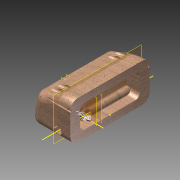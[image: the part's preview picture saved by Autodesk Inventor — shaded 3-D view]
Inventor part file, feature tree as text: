
AUTODESK INVENTOR PART (.ipt)
format: ipt  version: 2015 (Build 190159000, 159)  size: 325,120 bytes
history: native  units: in
note: dims shown in document units (in); Inventor stores cm internally (conversion verified against a paired STEP export)
features: extrude x8, sketch x6, fillet x4, plane x4, hole x2, reference x2, projected_geometry x1
ambient origin geometry x8: Origin, YZ Plane, XZ Plane, XY Plane, X Axis, Y Axis, Z Axis, Center Point
bodies: Solid1 (feature_tree)
feature tree (27):
  sketch  "Sketch1"  dims[d0=3.17in d1=1.53in d2=1.6in d3=0.0in]
  extrude  "Extrusion1"  Depth=1.53in
  fillet  "Fillet3"  Radius=1.6in
  sketch  "Sketch5"  dims[d20=1.1in d22=1.4in d25=1.15in d26=1.25in]
  extrude  "Extrusion5"  Depth=1.4in
  fillet  "Fillet4"  Radius=1.15in
  fillet  "Fillet5"  Radius=1.25in
  extrude  "Extrusion6"  Depth=0.09in
  fillet  "Fillet6"  Radius=0.13in
  plane  "Work Plane1"
  hole  "Hole1"  [1 undecoded]
  extrude  "Extrusion8"  Depth=0.3in
  hole  "Hole2"  [1 undecoded]
  plane  "Work Plane2"
  plane  "Work Plane3"
  sketch  "Sketch9"  dims[d34=0.2in d35=0.3in]
  extrude  "Extrusion9"  Depth=0.2in
  extrude  "Extrusion10"  Depth=0.27in
  plane  "Work Plane4"
  extrude  "Extrusion11"  Depth=2.0in
  sketch  "Sketch7"  dims[d30=1.0in d31=0.0in d33=0.3in]
  sketch  "Sketch10"  dims[d36=1.0in d37=0.0in d39=2.4in d40=0.93in d42=0.0in d43=0.57in d45=0.2in d46=0.27in d47=2.0in d48=1.35in d49=0.2in d50=0.75in d51=0.375in d52=0.25in d53=0.5635in d54=1.0in d55=0.8108in d56=0.3in d57=0.06in d58=1.0in d59=0.0in d60=0.3in d61=0.5in d62=0.29in d63=0.75in d64=0.375in d65=0.25in d66=0.5635in d67=0.35in d68=0.8108in d70=-0.5in d71=-1.0in d72=0.05in d73=0.05in d74=0.3in d75=0.3in d76=0.27in d77=0.0in d78=0.27in d79=0.0in d80=-0.2in d81=0.32in d82=0.33in d83=1.0in d84=0.0in]
  projected_geometry  "Projected Loop1"
  reference  "Reference1"
  reference  "Reference2"
  sketch  "Sketch6"  dims[d27=0.2in d28=0.09in d29=0.13in]
  extrude  "Extrusion7"  Depth=1.35in
note: 2 required parameter values undecoded (feature->parameter linkage not recoverable at this tier; creation-order binding heuristic only, values carry confidence <= 0.55)
